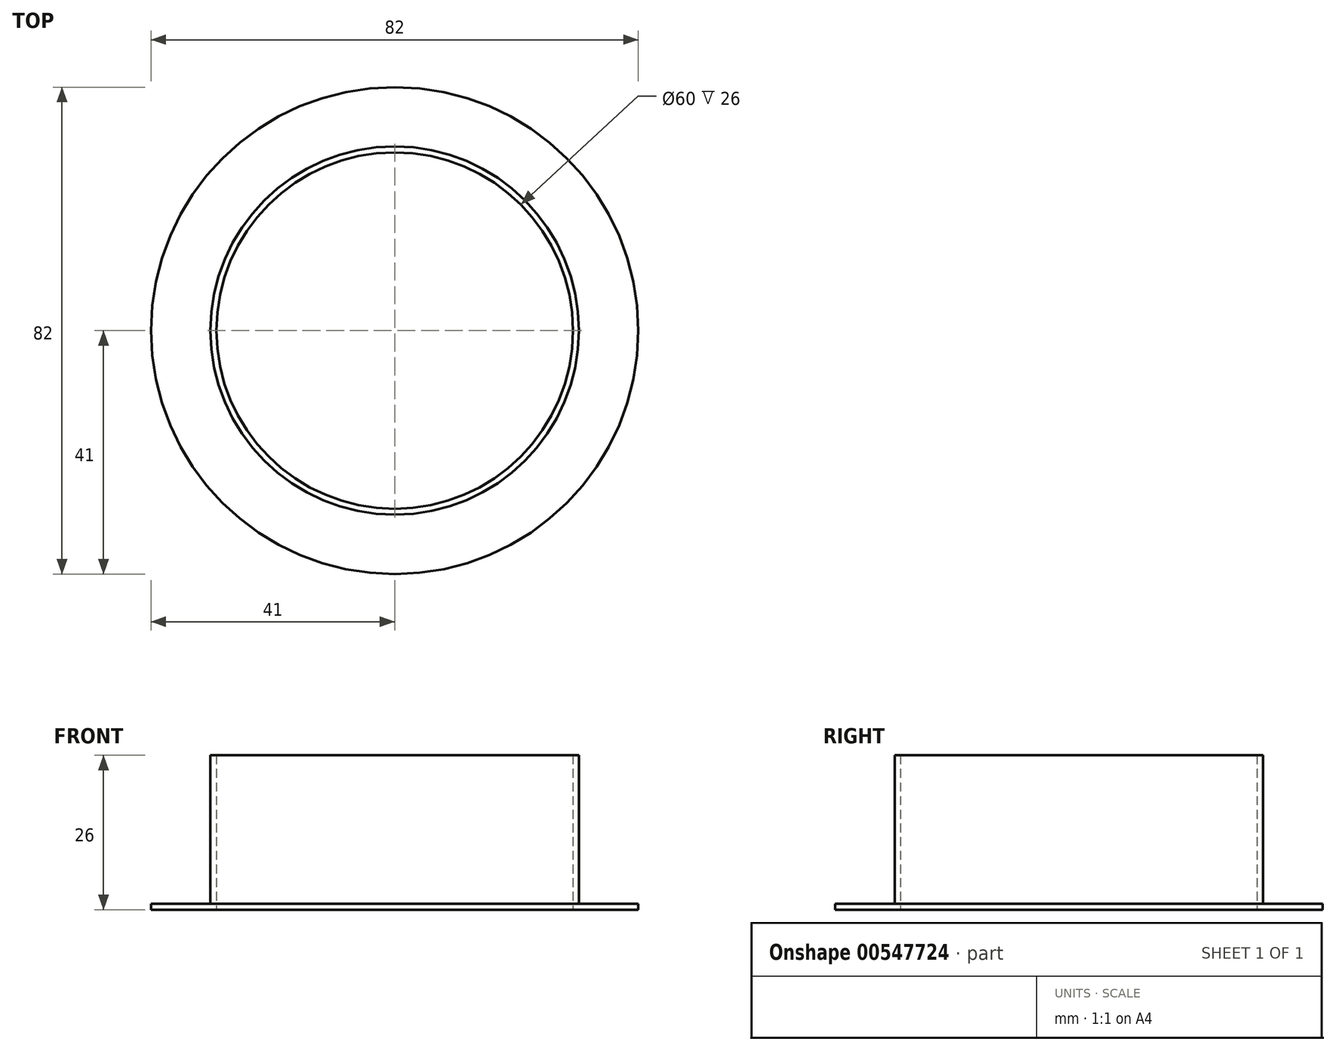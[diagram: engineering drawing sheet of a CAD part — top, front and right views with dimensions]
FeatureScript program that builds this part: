
annotation { "Feature Type Name" : "Feature", "Feature Type Description" : "" }
export const myFeature = defineFeature(function(context is Context, id is Id, definition is map)
    precondition{}
    {
        {
            var Q0;
            Q0=qCreatedBy(makeId("Front.planeOp"),FACE);
            var sketch = newSketch(context, id + "F0", { "sketchPlane" : qUnion([Q0])});
            skLineSegment(sketch, "E0", {"start": v(0, 0) * mm, "end": v(0, 50.15) * mm, "construction": true});
            skLineSegment(sketch, "E1", {"start": v(-41, 0) * mm, "end": v(-41, 1) * mm});
            skLineSegment(sketch, "E2", {"start": v(-41, 1) * mm, "end": v(-31, 1) * mm});
            skLineSegment(sketch, "E3", {"start": v(-31, 1) * mm, "end": v(-31, 26) * mm});
            skLineSegment(sketch, "E4", {"start": v(-31, 26) * mm, "end": v(-30, 26) * mm});
            skLineSegment(sketch, "E5", {"start": v(-30, 26) * mm, "end": v(-30, 0) * mm});
            skLineSegment(sketch, "E6", {"start": v(-30, 0) * mm, "end": v(-41, 0) * mm});
            skSolve(sketch);
        }
        {
            var Q0;
            Q0 = qSketchRegion(id + "F0", true);
            var Q1;
            Q1=sQuery(id+"F0.wireOp",EDGE,"E0");
            revolve(context, id + "F1", {"surfaceOperationType" : NewSurfaceOperationType.NEW, "entities" : qUnion([Q0]), "axis" : qUnion([Q1]), "revolveType" : RevolveType.FULL});
        }
    });
